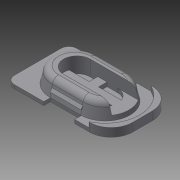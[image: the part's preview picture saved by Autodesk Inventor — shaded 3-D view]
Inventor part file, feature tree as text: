
AUTODESK INVENTOR PART (.ipt)
format: ipt  version: 2014 SP1 (Build 180222100, 222)  size: 1,671,168 bytes
history: native  units: in
note: dims shown in document units (in); Inventor stores cm internally (conversion verified against a paired STEP export)
features: extrude x7, sketch x7, projected_geometry x6, fillet x3, plane x1, mirror x1, other x1
ambient origin geometry x8: Origin, YZ Plane, XZ Plane, XY Plane, X Axis, Y Axis, Z Axis, Center Point
bodies: Solid1 (feature_tree)
feature tree (26):
  extrude  "Extrusion1"  Depth=1.25in
  extrude  "Extrusion2"  Depth=0.3615in
  fillet  "Fillet1"  Radius=0.3615in
  extrude  "Extrusion3"  Depth=0.574in
  extrude  "Extrusion4"  Depth=0.041in TaperAngle=0.0deg
  extrude  "Extrusion5"  Depth=0.4955in
  extrude  "Extrusion6"  Depth=0.01in
  fillet  "Fillet2"  Radius=0.1465in
  fillet  "Fillet3"  Radius=0.1465in
  plane  "Work Plane1"
  extrude  "Extrusion7"  Depth=0.3105in
  mirror  "Mirror1"
  sketch  "Sketch1"  dims[d1=0.732in d4=1.2245in d5=1.25in]
  other  "Image1"
  sketch  "Sketch2"  dims[d8=0.25in d9=0.0938in d10=0.3615in]
  projected_geometry  "Projected Loop1"
  sketch  "Sketch3"  dims[d11=0.4375in d12=0.574in]
  projected_geometry  "Projected Loop2"
  sketch  "Sketch4"  dims[d15=0.732in d16=0.041in d17=0.0in]
  projected_geometry  "Projected Loop3"
  sketch  "Sketch5"  dims[d18=0.1925in d19=0.4955in]
  projected_geometry  "Projected Loop4"
  sketch  "Sketch6"  dims[d20=0.097in d21=0.0in d22=0.01in d23=0.1465in d24=0.1465in]
  projected_geometry  "Projected Loop5"
  sketch  "Sketch7"  dims[d25=0.181in d26=-0.0825in d27=0.3105in d28=0.158in d29=0.1335in d30=0.0in d31=0.1325in d32=0.1085in d33=0.1085in d36=0.1335in d37=0.0in d38=0.033in d39=0.0575in d40=0.0in d41=0.003in d42=0.075in d43=0.102in d45=0.0575in d46=0.0in]
  projected_geometry  "Project Cut Edges1"
